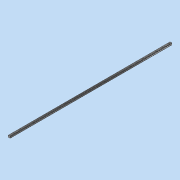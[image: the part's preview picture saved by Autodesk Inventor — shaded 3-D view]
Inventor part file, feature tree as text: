
AUTODESK INVENTOR PART (.ipt)
format: ipt  version: 2021 (Build 250183000, 183)  size: 276,992 bytes
history: native  units: mm
features: extrude x3, sketch x2, projected_geometry x1
ambient origin geometry x8: Origin, YZ Plane, XZ Plane, XY Plane, X Axis, Y Axis, Z Axis, Center Point
bodies: Solid1 (feature_tree)
feature tree (6):
  extrude  "Extrusion1"  Depth=1500.0mm
  sketch  "Sketch2"  dims[d4=6.0mm d6=9.5mm d7=6.0mm d9=9.5mm d10=6.0mm d12=9.5mm d13=6.0mm d15=9.5mm d16=6.0mm d18=9.5mm d19=6.0mm d21=9.5mm d22=6.0mm d24=9.5mm d25=6.0mm d27=9.5mm d28=6.0mm d30=9.5mm d31=6.0mm d33=9.5mm d34=6.0mm d36=9.5mm d37=6.0mm d39=9.5mm d40=6.0mm d42=9.5mm d43=6.0mm d45=9.5mm d46=6.0mm d48=9.5mm d49=6.0mm d51=9.5mm d52=6.0mm d54=9.5mm d55=6.0mm d57=9.5mm d58=6.0mm d60=9.5mm d61=6.0mm d63=9.5mm d64=6.0mm d66=9.5mm d67=6.0mm d69=9.5mm d70=6.0mm d72=9.5mm d73=6.0mm d75=9.5mm d76=6.0mm d78=30.0mm d79=0.0mm d80=8.4mm d81=0.0mm]
  extrude  "Extrusion2"  Depth=8.4mm
  extrude  "Extrusion3"  Depth=8.4mm
  sketch  "Sketch1"  dims[d0=1500.0mm d1=0.0mm d3=9.5mm]
  projected_geometry  "Projected Loop1"
